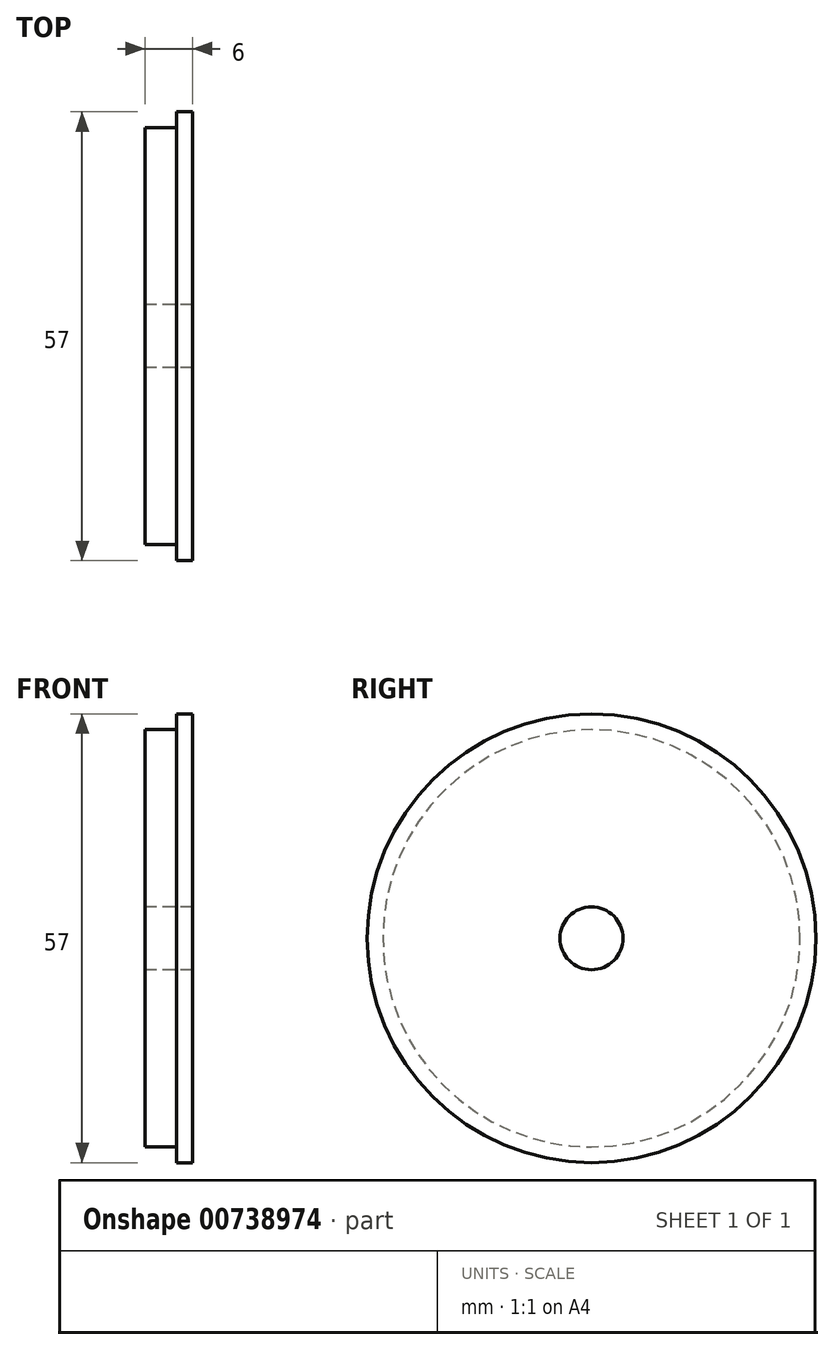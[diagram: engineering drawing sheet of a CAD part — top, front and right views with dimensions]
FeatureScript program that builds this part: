
annotation { "Feature Type Name" : "Feature", "Feature Type Description" : "" }
export const myFeature = defineFeature(function(context is Context, id is Id, definition is map)
    precondition{}
    {
        {
            var Q0;
            Q0=qCreatedBy(makeId("Right.planeOp"),FACE);
            var sketch = newSketch(context, id + "F0", { "sketchPlane" : qUnion([Q0])});
            skCircle(sketch, "E0", {"center": v(0, 0) * mm, "radius": 28.5 * mm});
            skCircle(sketch, "E1", {"center": v(0, 0) * mm, "radius": 26.5 * mm});
            skCircle(sketch, "E2", {"center": v(0, 0) * mm, "radius": 4 * mm});
            skSolve(sketch);
        }
        {
            var Q0;
            Q0=makeQuery(id+"F0.imprint","IMPRINT",FACE,{"disambiguationData":[TD([[makeQuery(id+"F0.imprint","IMPRINT",EDGE,{"derivedFrom":sQuery(id+"F0.wireOp",EDGE,"E1")}),1.0]])]});
            var Q1;
            Q1=makeQuery(id+"F0.imprint","IMPRINT",FACE,{"disambiguationData":[TD([[makeQuery(id+"F0.imprint","IMPRINT",EDGE,{"derivedFrom":sQuery(id+"F0.wireOp",EDGE,"E0")}),1.0]])]});
            extrude(context, id + "F1", {"entities" : qUnion([Q0, Q1]), "depth" : 6 * mm, "offsetDistance" : 25 * mm});
        }
        {
            var Q0;
            Q0 = qSketchRegion(id + "F0", true);
            extrude(context, id + "F2", {"entities" : qUnion([Q0]), "operationType" : NewBodyOperationType.REMOVE, "depth" : 4 * mm, "offsetDistance" : 25 * mm});
        }
    });
